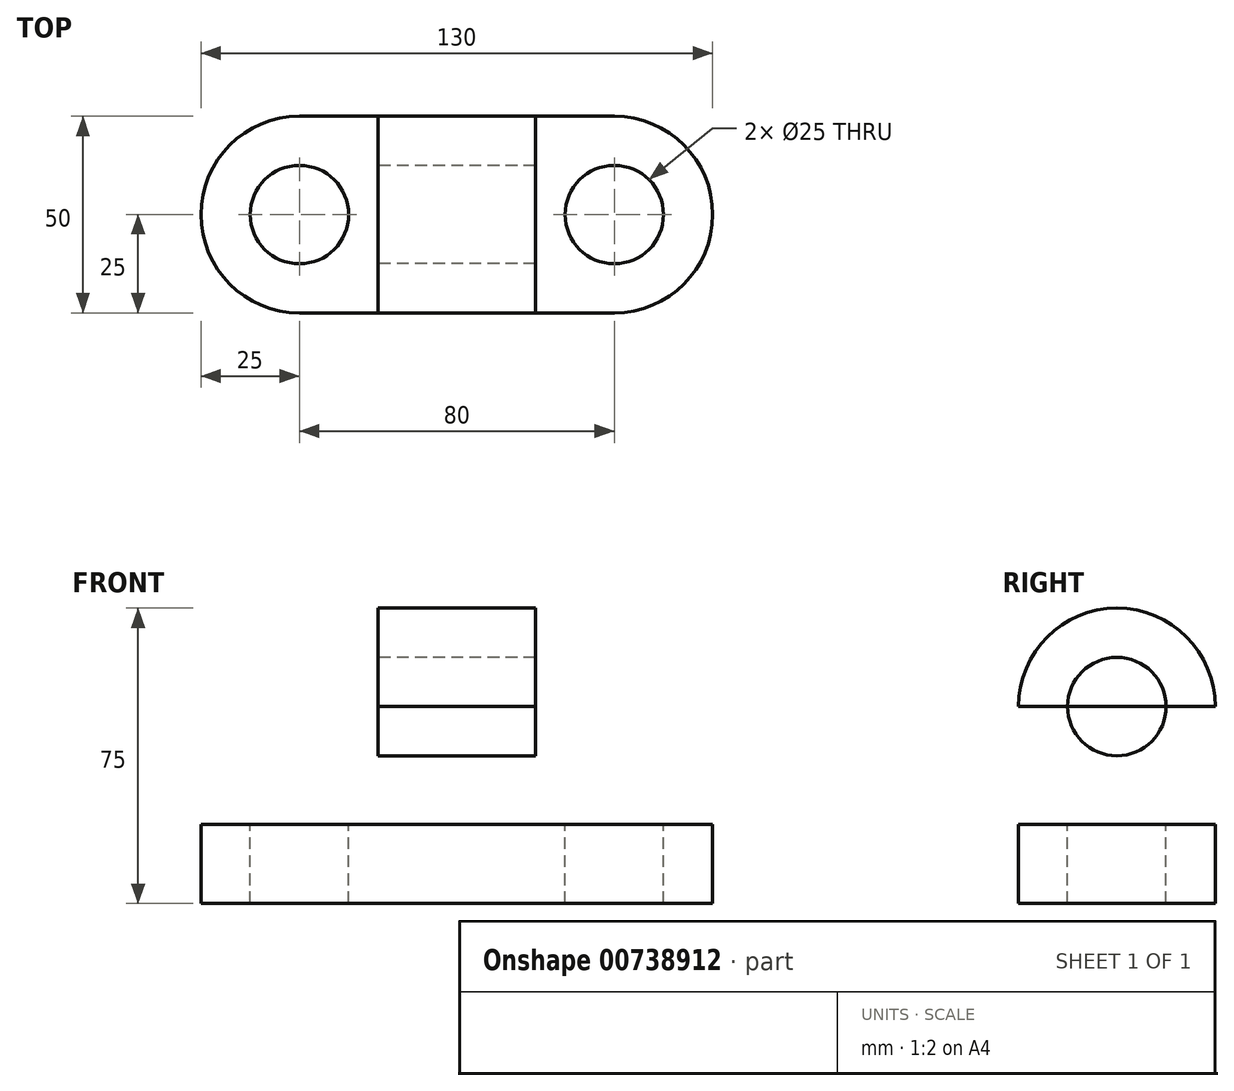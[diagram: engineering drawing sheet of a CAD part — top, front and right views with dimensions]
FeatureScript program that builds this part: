
annotation { "Feature Type Name" : "Feature", "Feature Type Description" : "" }
export const myFeature = defineFeature(function(context is Context, id is Id, definition is map)
    precondition{}
    {
        {
            var Q0;
            Q0=qCreatedBy(makeId("Top.planeOp"),FACE);
            var sketch = newSketch(context, id + "F0", { "sketchPlane" : qUnion([Q0])});
            skLineSegment(sketch, "E0", {"start": v(0, 0) * mm, "end": v(60, 0) * mm});
            skLineSegment(sketch, "E1", {"start": v(60, 0) * mm, "end": v(60, -50) * mm, "construction": true});
            skLineSegment(sketch, "E2", {"start": v(60, -50) * mm, "end": v(-20, -50) * mm});
            skLineSegment(sketch, "E3", {"start": v(-20, -50) * mm, "end": v(-20, 0) * mm, "construction": true});
            skArc(sketch, "E4", {"start": v(60, -50) * mm, "mid": v(85, -25) * mm, "end": v(60, 0) * mm});
            skArc(sketch, "E5", {"start": v(-20, 0) * mm, "mid": v(-45, -25) * mm, "end": v(-20, -50) * mm});
            skLineSegment(sketch, "E6", {"start": v(0, 0) * mm, "end": v(0, -50) * mm});
            skLineSegment(sketch, "E7", {"start": v(40, 0) * mm, "end": v(40, -50) * mm});
            skLineSegment(sketch, "E8", {"start": v(0, -25) * mm, "end": v(-20, -25) * mm, "construction": true});
            skLineSegment(sketch, "E9", {"start": v(60, -25) * mm, "end": v(40, -25) * mm, "construction": true});
            skCircle(sketch, "E10", {"center": v(-20, -25) * mm, "radius": 12.5 * mm});
            skCircle(sketch, "E11", {"center": v(60, -25) * mm, "radius": 12.5 * mm});
            skLineSegment(sketch, "E12", {"start": v(0, 0) * mm, "end": v(-20, 0) * mm});
            skSolve(sketch);
        }
        {
            var Q0;
            Q0 = qSketchRegion(id + "F0", true);
            extrude(context, id + "F1", {"entities" : qUnion([Q0]), "oppositeDirection" : true, "depth" : 20 * mm, "offsetDistance" : 25 * mm});
        }
        {
            var Q0;
            {var subQ0=sQuery(id+"F0.wireOp",EDGE,"E6");Q0=makeQuery(id+"F0.imprint","IMPRINT",FACE,{"disambiguationData":[TD([[makeQuery(id+"F0.imprint","IMPRINT",EDGE,{"derivedFrom":subQ0}),1.0]])]});}
            extrude(context, id + "F2", {"entities" : qUnion([Q0]), "operationType" : NewBodyOperationType.ADD, "depth" : 30 * mm, "offsetDistance" : 25 * mm});
        }
        {
            var Q0;
            Q0=qCreatedBy(makeId("Right.planeOp"),FACE);
            var sketch = newSketch(context, id + "F3", { "sketchPlane" : qUnion([Q0])});
            skLineSegment(sketch, "E13", {"start": v(0, 0) * mm, "end": v(0, 30) * mm});
            skLineSegment(sketch, "E14", {"start": v(0, 30) * mm, "end": v(-50, 30) * mm});
            skLineSegment(sketch, "E15", {"start": v(-50, 30) * mm, "end": v(-50, 0) * mm});
            skLineSegment(sketch, "E16", {"start": v(-50, 0) * mm, "end": v(0, 0) * mm});
            skArc(sketch, "E17", {"start": v(0, 30) * mm, "mid": v(-25, 55) * mm, "end": v(-50, 30) * mm});
            skPoint(sketch, "E18", {"position": v(-25, 0) * mm});
            skLineSegment(sketch, "E19", {"start": v(-25, 30) * mm, "end": v(-25, 0) * mm, "construction": true});
            skCircle(sketch, "E20", {"center": v(-25, 30) * mm, "radius": 12.5 * mm});
            skSolve(sketch);
        }
        {
            var Q0;
            Q0 = qSketchRegion(id + "F3", true);
            extrude(context, id + "F4", {"entities" : qUnion([Q0]), "operationType" : NewBodyOperationType.ADD, "depth" : 40 * mm, "offsetDistance" : 25 * mm});
        }
        {
            var Q0;
            {var subQ0=sQuery(id+"F3.wireOp",EDGE,"E20");var subQ1=sQuery(id+"F3.wireOp",EDGE,"E14");var subQ2=makeQuery(id+"F3.imprint","INTERSECT",VERTEX,{"disambiguationData":[OD(0.0)],"derivedFrom":[subQ1,subQ0]});Q0=makeQuery(id+"F3.imprint","IMPRINT",FACE,{"disambiguationData":[TD([[makeQuery(id+"F3.imprint","IMPRINT",EDGE,{"disambiguationData":[TD([[subQ2,-1.0]])],"derivedFrom":subQ1}),1.0]])]});}
            extrude(context, id + "F5", {"entities" : qUnion([Q0]), "operationType" : NewBodyOperationType.REMOVE, "endBound" : BoundingType.THROUGH_ALL, "depth" : 25 * mm, "offsetDistance" : 25 * mm});
        }
    });
